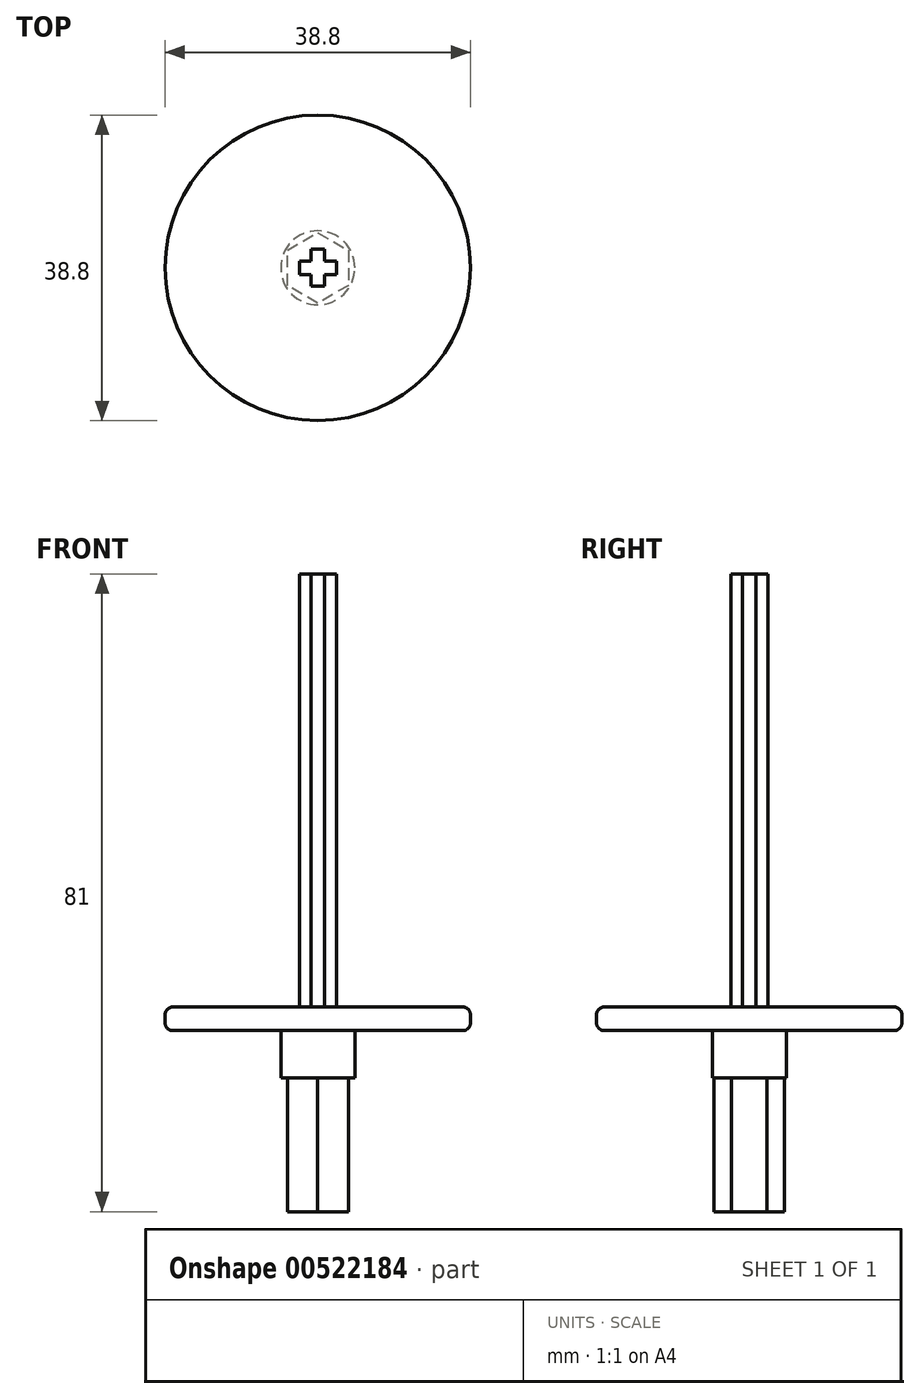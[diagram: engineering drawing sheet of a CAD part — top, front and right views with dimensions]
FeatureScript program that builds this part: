
annotation { "Feature Type Name" : "Feature", "Feature Type Description" : "" }
export const myFeature = defineFeature(function(context is Context, id is Id, definition is map)
    precondition{}
    {
        {
            var Q0;
            Q0=qCreatedBy(makeId("Top.planeOp"),FACE);
            var sketch = newSketch(context, id + "F0", { "sketchPlane" : qUnion([Q0])});
            skCircle(sketch, "E0.cCircle", {"center": v(0, 0) * mm, "radius": 3.88 * mm, "construction": true});
            skLineSegment(sketch, "E0.0", {"start": v(3.88, 2.24) * mm, "end": v(3.88, -2.24) * mm});
            skLineSegment(sketch, "E0.1", {"start": v(3.88, -2.24) * mm, "end": v(0, -4.47) * mm});
            skLineSegment(sketch, "E0.2", {"start": v(0, -4.47) * mm, "end": v(-3.87, -2.24) * mm});
            skLineSegment(sketch, "E0.3", {"start": v(-3.87, -2.24) * mm, "end": v(-3.88, 2.24) * mm});
            skLineSegment(sketch, "E0.4", {"start": v(-3.88, 2.24) * mm, "end": v(0, 4.47) * mm});
            skLineSegment(sketch, "E0.5", {"start": v(0, 4.47) * mm, "end": v(3.88, 2.24) * mm});
            skPoint(sketch, "E0.0.midPoint", {"position": v(3.88, 0) * mm});
            skSolve(sketch);
        }
        {
            var Q0;
            Q0=makeQuery(id+"F0.imprint","IMPRINT",FACE,{"disambiguationData":[TD([[makeQuery(id+"F0.imprint","IMPRINT",EDGE,{"derivedFrom":sQuery(id+"F0.wireOp",EDGE,"E0.0")}),-1.0]])]});
            extrude(context, id + "F1", {"entities" : qUnion([Q0]), "oppositeDirection" : true, "depth" : 17 * mm, "offsetDistance" : 25 * mm});
        }
        {
            var Q0;
            Q0=makeQuery(id+"F1.opExtrude","CAP_FACE",FACE,{"disambiguationData":[OSD([sQuery(id+"F0.wireOp",EDGE,"E0.0"),sQuery(id+"F0.wireOp",EDGE,"E0.1"),sQuery(id+"F0.wireOp",EDGE,"E0.2"),sQuery(id+"F0.wireOp",EDGE,"E0.3"),sQuery(id+"F0.wireOp",EDGE,"E0.4"),sQuery(id+"F0.wireOp",EDGE,"E0.5")])],"isStart":true});
            var sketch = newSketch(context, id + "F2", { "sketchPlane" : qUnion([Q0])});
            skCircle(sketch, "E1", {"center": v(0, 0) * mm, "radius": 4.7 * mm});
            skSolve(sketch);
        }
        {
            var Q0;
            Q0 = qSketchRegion(id + "F2", true);
            extrude(context, id + "F3", {"entities" : qUnion([Q0]), "operationType" : NewBodyOperationType.ADD, "depth" : 6 * mm, "offsetDistance" : 25 * mm});
        }
        {
            var Q0;
            Q0=makeQuery(id+"F3.opExtrude","CAP_FACE",FACE,{"disambiguationData":[OSD([sQuery(id+"F2.wireOp",EDGE,"E1")])],"isStart":false});
            var sketch = newSketch(context, id + "F4", { "sketchPlane" : qUnion([Q0])});
            skCircle(sketch, "E2", {"center": v(0, 0) * mm, "radius": 19.4 * mm});
            skSolve(sketch);
        }
        {
            var Q0;
            Q0 = qSketchRegion(id + "F4", true);
            extrude(context, id + "F5", {"entities" : qUnion([Q0]), "operationType" : NewBodyOperationType.ADD, "depth" : 3 * mm, "offsetDistance" : 25 * mm});
        }
        {
            var Q0;
            Q0=makeQuery(id+"F5.opExtrude","CAP_FACE",FACE,{"disambiguationData":[OSD([sQuery(id+"F4.wireOp",EDGE,"E2")])],"isStart":false});
            var sketch = newSketch(context, id + "F6", { "sketchPlane" : qUnion([Q0])});
            skLineSegment(sketch, "E3.bottom", {"start": v(-0.85, 2.35) * mm, "end": v(0.85, 2.35) * mm});
            skLineSegment(sketch, "E3.top", {"start": v(-0.85, -2.35) * mm, "end": v(0.85, -2.35) * mm});
            skLineSegment(sketch, "E3.left", {"start": v(-0.85, 2.35) * mm, "end": v(-0.85, -2.35) * mm});
            skLineSegment(sketch, "E3.right", {"start": v(0.85, 2.35) * mm, "end": v(0.85, -2.35) * mm});
            skPoint(sketch, "E3.middle", {"position": v(0, 0) * mm});
            skLineSegment(sketch, "E4.bottom", {"start": v(-2.35, 0.85) * mm, "end": v(2.35, 0.85) * mm});
            skLineSegment(sketch, "E4.top", {"start": v(-2.35, -0.85) * mm, "end": v(2.35, -0.85) * mm});
            skLineSegment(sketch, "E4.left", {"start": v(-2.35, 0.85) * mm, "end": v(-2.35, -0.85) * mm});
            skLineSegment(sketch, "E4.right", {"start": v(2.35, 0.85) * mm, "end": v(2.35, -0.85) * mm});
            skSolve(sketch);
        }
        {
            var Q0;
            {var subQ5=sQuery(id+"F6.wireOp",EDGE,"E4.left");Q0=makeQuery(id+"F6.imprint","IMPRINT",FACE,{"disambiguationData":[TD([[makeQuery(id+"F6.imprint","IMPRINT",EDGE,{"derivedFrom":subQ5}),1.0]])]});}
            var Q1;
            {var subQ0=sQuery(id+"F6.wireOp",EDGE,"E3.bottom");Q1=makeQuery(id+"F6.imprint","IMPRINT",FACE,{"disambiguationData":[TD([[makeQuery(id+"F6.imprint","IMPRINT",EDGE,{"derivedFrom":subQ0}),-1.0]])]});}
            var Q2;
            {var subQ0=sQuery(id+"F6.wireOp",EDGE,"E4.bottom");var subQ1=sQuery(id+"F6.wireOp",EDGE,"E3.left");var subQ2=makeQuery(id+"F6.imprint","INTERSECT",VERTEX,{"derivedFrom":[subQ1,subQ0]});Q2=makeQuery(id+"F6.imprint","IMPRINT",FACE,{"disambiguationData":[TD([[makeQuery(id+"F6.imprint","IMPRINT",EDGE,{"disambiguationData":[TD([[subQ2,-1.0]])],"derivedFrom":subQ1}),1.0]])]});}
            var Q3;
            {var subQ5=sQuery(id+"F6.wireOp",EDGE,"E4.right");Q3=makeQuery(id+"F6.imprint","IMPRINT",FACE,{"disambiguationData":[TD([[makeQuery(id+"F6.imprint","IMPRINT",EDGE,{"derivedFrom":subQ5}),-1.0]])]});}
            var Q4;
            {var subQ0=sQuery(id+"F6.wireOp",EDGE,"E3.top");Q4=makeQuery(id+"F6.imprint","IMPRINT",FACE,{"disambiguationData":[TD([[makeQuery(id+"F6.imprint","IMPRINT",EDGE,{"derivedFrom":subQ0}),1.0]])]});}
            extrude(context, id + "F7", {"entities" : qUnion([Q0, Q1, Q2, Q3, Q4]), "operationType" : NewBodyOperationType.ADD, "depth" : 55 * mm, "offsetDistance" : 25 * mm});
        }
        {
            var Q0;
            Q0=makeQuery(id+"F5.opExtrude","CAP_EDGE",EDGE,{"disambiguationData":[OSD([sQuery(id+"F4.wireOp",EDGE,"E2")])],"isStart":true});
            var Q1;
            Q1=makeQuery(id+"F5.opExtrude","CAP_EDGE",EDGE,{"disambiguationData":[OSD([sQuery(id+"F4.wireOp",EDGE,"E2")])],"isStart":false});
            fillet(context, id + "F8", {"entities" : qUnion([Q0, Q1]), "radius" : 1 * mm, "tangentPropagation" : true, "allowEdgeOverflow" : false});
        }
    });
